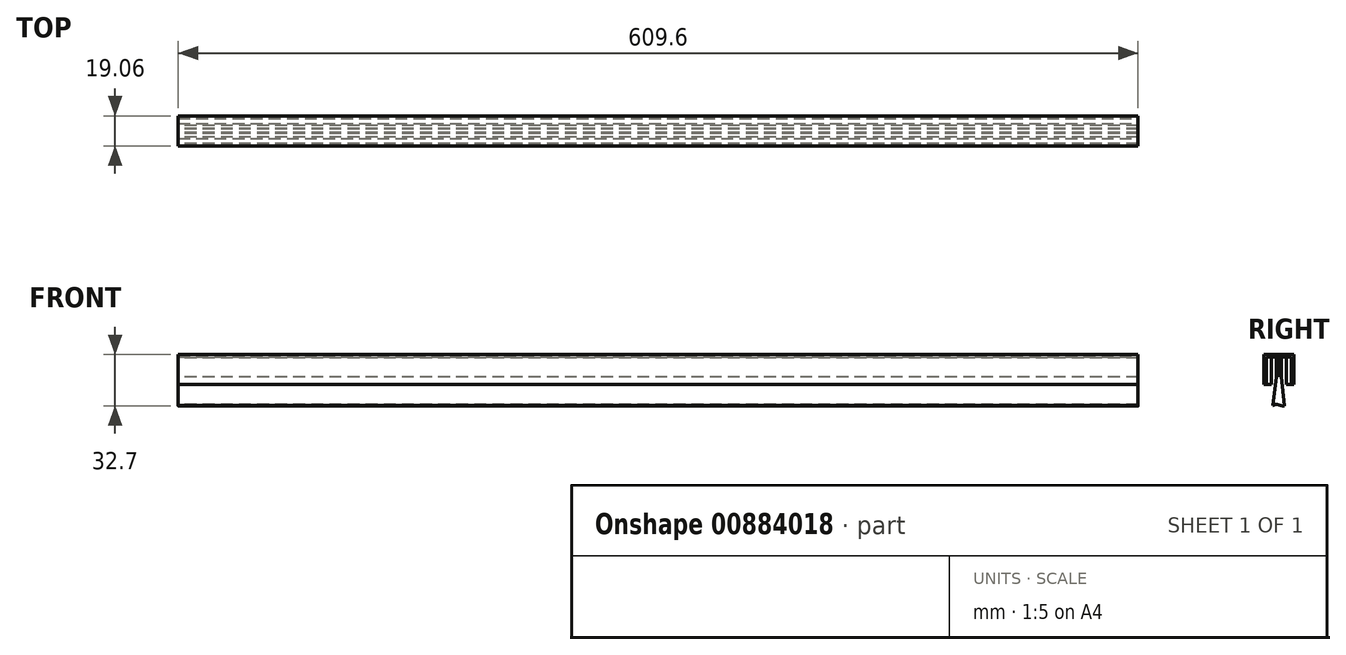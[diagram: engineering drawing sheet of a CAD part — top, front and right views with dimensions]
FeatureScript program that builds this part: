
annotation { "Feature Type Name" : "Feature", "Feature Type Description" : "" }
export const myFeature = defineFeature(function(context is Context, id is Id, definition is map)
    precondition{}
    {
        {
            var Q0;
            Q0=qCreatedBy(makeId("Right.planeOp"),FACE);
            var sketch = newSketch(context, id + "F0", { "sketchPlane" : qUnion([Q0])});
            skLineSegment(sketch, "E0.top", {"start": v(0.83, 6.35) * mm, "end": v(-0.83, 6.35) * mm});
            skLineSegment(sketch, "E0.left", {"start": v(1.59, -6.35) * mm, "end": v(1.59, 5.59) * mm});
            skLineSegment(sketch, "E0.right", {"start": v(-1.59, -6.35) * mm, "end": v(-1.59, 5.59) * mm});
            skPoint(sketch, "E0.middle", {"position": v(0, 0) * mm});
            skLineSegment(sketch, "E1.left", {"start": v(1.08, -6.35) * mm, "end": v(1.08, 5.59) * mm});
            skLineSegment(sketch, "E1.right", {"start": v(-1.08, -6.35) * mm, "end": v(-1.08, 5.59) * mm});
            skLineSegment(sketch, "E2.trimOffspring", {"start": v(-0.83, 5.84) * mm, "end": v(0.83, 5.84) * mm});
            skLineSegment(sketch, "E3", {"start": v(-1.59, -6.35) * mm, "end": v(-3.83, -24.43) * mm});
            skLineSegment(sketch, "E4", {"start": v(1.59, -6.35) * mm, "end": v(3.53, -24.5) * mm});
            skLineSegment(sketch, "E5", {"start": v(-1.59, -6.35) * mm, "end": v(-1.08, -6.35) * mm});
            skLineSegment(sketch, "E6.trimOffspring", {"start": v(1.08, -6.35) * mm, "end": v(1.59, -6.35) * mm});
            skFitSpline(sketch, "E7", {"points": [v(-3.83, -24.43) * mm, v(-0.96, -23.8) * mm, v(1.97, -24.72) * mm, v(3.53, -24.5) * mm], "startDerivative": vector(7.76, 3.1) * mm, "endDerivative": vector(5.43, 1.8) * mm});
            skPoint(sketch, "E8.visualSharp", {"position": v(-1.08, 5.84) * mm});
            skArc(sketch, "E8.filletArc", {"start": v(-0.83, 5.84) * mm, "mid": v(-1, 5.77) * mm, "end": v(-1.08, 5.59) * mm});
            skPoint(sketch, "E9.visualSharp", {"position": v(1.08, 5.84) * mm});
            skArc(sketch, "E9.filletArc", {"start": v(1.08, 5.59) * mm, "mid": v(1, 5.77) * mm, "end": v(0.83, 5.84) * mm});
            skPoint(sketch, "E10.visualSharp", {"position": v(-1.59, 6.35) * mm});
            skArc(sketch, "E10.filletArc", {"start": v(-0.83, 6.35) * mm, "mid": v(-1.36, 6.13) * mm, "end": v(-1.59, 5.59) * mm});
            skPoint(sketch, "E11.visualSharp", {"position": v(1.59, 6.35) * mm});
            skArc(sketch, "E11.filletArc", {"start": v(1.59, 5.59) * mm, "mid": v(1.36, 6.13) * mm, "end": v(0.83, 6.35) * mm});
            skSolve(sketch);
        }
        {
            var Q0;
            Q0=makeQuery(id+"F0.imprint","IMPRINT",FACE,{"disambiguationData":[TD([[makeQuery(id+"F0.imprint","IMPRINT",EDGE,{"derivedFrom":sQuery(id+"F0.wireOp",EDGE,"E1.left")}),1.0]])]});
            extrude(context, id + "F1", {"entities" : qUnion([Q0]), "depth" : 609.6 * mm, "offsetDistance" : 25.4 * mm});
        }
        {
            var Q0;
            Q0=makeQuery(id+"F0.imprint","IMPRINT",FACE,{"disambiguationData":[TD([[makeQuery(id+"F0.imprint","IMPRINT",EDGE,{"derivedFrom":sQuery(id+"F0.wireOp",EDGE,"E0.top")}),1.0]])]});
            extrude(context, id + "F2", {"entities" : qUnion([Q0]), "depth" : 609.6 * mm, "offsetDistance" : 25.4 * mm});
        }
        {
            var Q0;
            Q0=qCreatedBy(makeId("Right.planeOp"),FACE);
            var sketch = newSketch(context, id + "F3", { "sketchPlane" : qUnion([Q0])});
            skLineSegment(sketch, "E12", {"start": v(0, 13.93) * mm, "end": v(0, -12.76) * mm, "construction": true});
            skLineSegment(sketch, "E13.bottom", {"start": v(9.53, -11.1) * mm, "end": v(7.92, -11.1) * mm});
            skLineSegment(sketch, "E13.top", {"start": v(9.53, 7.95) * mm, "end": v(-9.53, 7.95) * mm});
            skLineSegment(sketch, "E13.left", {"start": v(9.53, -11.1) * mm, "end": v(9.53, 7.95) * mm});
            skLineSegment(sketch, "E13.right", {"start": v(-9.53, -11.1) * mm, "end": v(-9.53, 7.95) * mm});
            skPoint(sketch, "E13.middle", {"position": v(0, -1.57) * mm});
            skLineSegment(sketch, "E14.0", {"start": v(7.92, 6.35) * mm, "end": v(-7.92, 6.35) * mm});
            skLineSegment(sketch, "E14.1", {"start": v(7.92, -11.1) * mm, "end": v(7.92, 6.35) * mm});
            skLineSegment(sketch, "E14.3", {"start": v(-7.92, -11.1) * mm, "end": v(-7.92, 6.35) * mm});
            skLineSegment(sketch, "E15.trimOffspring", {"start": v(-7.92, -11.1) * mm, "end": v(-9.53, -11.1) * mm});
            skSolve(sketch);
        }
        {
            var Q0;
            Q0=makeQuery(id+"F3.imprint","IMPRINT",FACE,{"disambiguationData":[TD([[makeQuery(id+"F3.imprint","IMPRINT",EDGE,{"derivedFrom":sQuery(id+"F3.wireOp",EDGE,"E13.bottom")}),-1.0]])]});
            extrude(context, id + "F4", {"entities" : qUnion([Q0]), "depth" : 609.6 * mm, "offsetDistance" : 25.4 * mm});
        }
        {
            var Q0;
            Q0=makeQuery(id+"F4.opExtrude","CAP_FACE",FACE,{"disambiguationData":[OSD([sQuery(id+"F3.wireOp",EDGE,"E13.bottom"),sQuery(id+"F3.wireOp",EDGE,"E13.top"),sQuery(id+"F3.wireOp",EDGE,"E13.left"),sQuery(id+"F3.wireOp",EDGE,"E13.right"),sQuery(id+"F3.wireOp",EDGE,"E14.0"),sQuery(id+"F3.wireOp",EDGE,"E14.1"),sQuery(id+"F3.wireOp",EDGE,"E14.3"),sQuery(id+"F3.wireOp",EDGE,"E15.trimOffspring")])],"isStart":false});
            var sketch = newSketch(context, id + "F5", { "sketchPlane" : qUnion([Q0])});
            skLineSegment(sketch, "E16.bottom", {"start": v(-7.92, 6.35) * mm, "end": v(-4.75, 6.35) * mm});
            skLineSegment(sketch, "E16.top", {"start": v(-7.92, -11.1) * mm, "end": v(-4.75, -11.1) * mm});
            skLineSegment(sketch, "E16.left", {"start": v(-7.92, 6.35) * mm, "end": v(-7.92, -11.1) * mm});
            skLineSegment(sketch, "E16.right", {"start": v(-4.75, 6.35) * mm, "end": v(-4.75, -11.1) * mm});
            skLineSegment(sketch, "E17.bottom", {"start": v(7.92, 6.35) * mm, "end": v(4.75, 6.35) * mm});
            skLineSegment(sketch, "E17.top", {"start": v(7.92, -11.1) * mm, "end": v(4.75, -11.1) * mm});
            skLineSegment(sketch, "E17.left", {"start": v(7.92, 6.35) * mm, "end": v(7.92, -11.1) * mm});
            skLineSegment(sketch, "E17.right", {"start": v(4.75, 6.35) * mm, "end": v(4.75, -11.1) * mm});
            skSolve(sketch);
        }
        {
            var Q0;
            Q0=makeQuery(id+"F5.imprint","IMPRINT",FACE,{"disambiguationData":[TD([[makeQuery(id+"F5.imprint","IMPRINT",EDGE,{"derivedFrom":sQuery(id+"F5.wireOp",EDGE,"E16.bottom")}),1.0]])]});
            var Q1;
            Q1=makeQuery(id+"F5.imprint","IMPRINT",FACE,{"disambiguationData":[TD([[makeQuery(id+"F5.imprint","IMPRINT",EDGE,{"derivedFrom":sQuery(id+"F5.wireOp",EDGE,"E17.bottom")}),1.0]])]});
            extrude(context, id + "F6", {"entities" : qUnion([Q0, Q1]), "oppositeDirection" : true, "depth" : 609.6 * mm, "offsetDistance" : 25.4 * mm});
        }
    });
